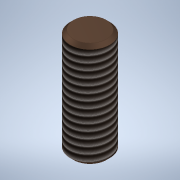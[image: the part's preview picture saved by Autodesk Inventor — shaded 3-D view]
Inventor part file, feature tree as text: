
AUTODESK INVENTOR PART (.ipt)
format: ipt  version: 2020 (Build 240168000, 168)  size: 114,688 bytes
history: native  units: mm
features: chamfer x2, extrude x1, thread x1, sketch x1
ambient origin geometry x8: Origin, YZ Plane, XZ Plane, XY Plane, X Axis, Y Axis, Z Axis, Center Point
bodies: Solid1 (feature_tree)
feature tree (5):
  extrude  "Extrusion1"  Depth=15.9mm TaperAngle=0.0deg
  chamfer  "Chamfer1"  Distance=0.5mm Angle=45.0deg
  chamfer  "Chamfer2"  Distance=0.5mm Angle=45.0deg
  thread  "Thread1"  [1 undecoded]
  sketch  "Sketch1"  dims[d0=6.0mm d1=15.9mm d2=0.0mm d3=0.5mm d4=2.0mm d5=45.0deg d6=0.5mm d7=2.0mm d8=45.0deg d9=14.9mm d10=0.0mm]
note: 1 required parameter value undecoded (feature->parameter linkage not recoverable at this tier; creation-order binding heuristic only, values carry confidence <= 0.55)
